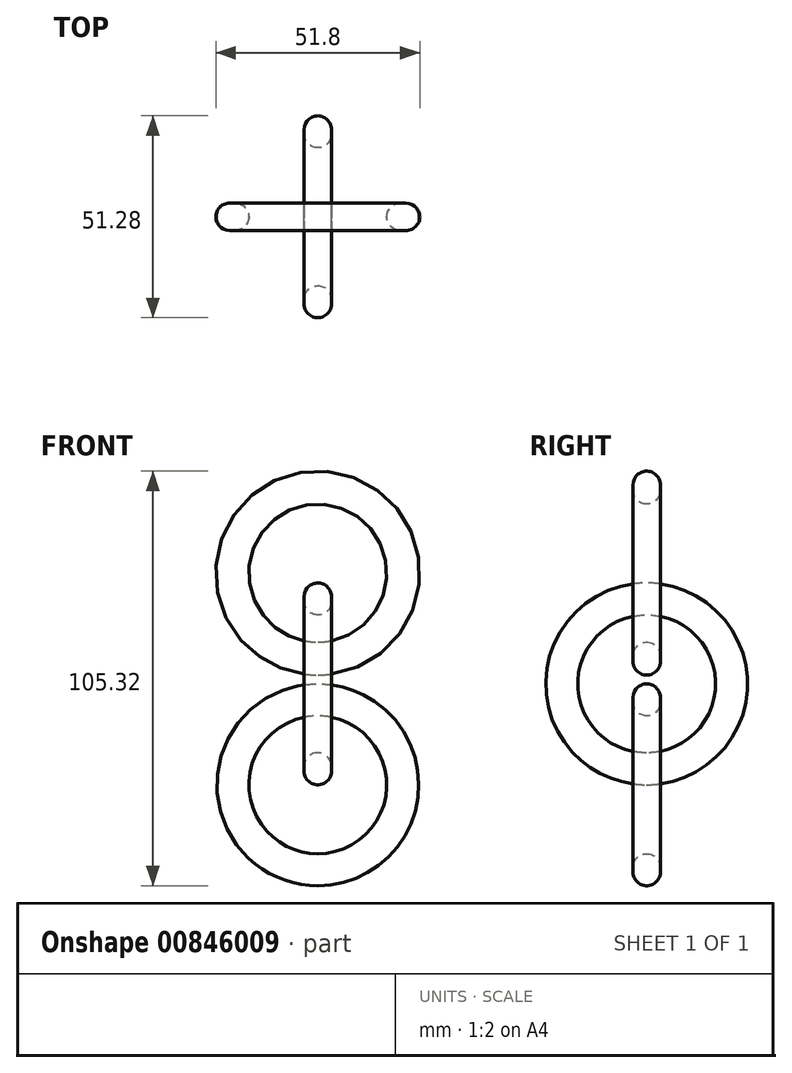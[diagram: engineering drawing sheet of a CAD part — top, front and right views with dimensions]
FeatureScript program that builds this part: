
annotation { "Feature Type Name" : "Feature", "Feature Type Description" : "" }
export const myFeature = defineFeature(function(context is Context, id is Id, definition is map)
    precondition{}
    {
        {
            var Q0;
            Q0=qCreatedBy(makeId("Right.planeOp"),FACE);
            var sketch = newSketch(context, id + "F0", { "sketchPlane" : qUnion([Q0])});
            skCircle(sketch, "E0", {"center": v(0, 0) * mm, "radius": 25.64 * mm});
            skCircle(sketch, "E1", {"center": v(0, 0) * mm, "radius": 17.51 * mm});
            skSolve(sketch);
        }
        {
            var Q0;
            Q0=makeQuery(id+"F0.imprint","IMPRINT",FACE,{"disambiguationData":[TD([[makeQuery(id+"F0.imprint","IMPRINT",EDGE,{"derivedFrom":sQuery(id+"F0.wireOp",EDGE,"E0")}),1.0]])]});
            extrude(context, id + "F1", {"entities" : qUnion([Q0]), "endBound" : BoundingType.SYMMETRIC, "depth" : 7 * mm, "offsetDistance" : 25 * mm});
        }
        {
            var Q0;
            Q0=qCreatedBy(makeId("Front.planeOp"),FACE);
            var sketch = newSketch(context, id + "F2", { "sketchPlane" : qUnion([Q0])});
            skCircle(sketch, "E2", {"center": v(0, -25.64) * mm, "radius": 25.64 * mm});
            skCircle(sketch, "E3", {"center": v(0, -25.64) * mm, "radius": 17.5 * mm});
            skSolve(sketch);
        }
        {
            var Q0;
            Q0=makeQuery(id+"F2.imprint","IMPRINT",FACE,{"disambiguationData":[TD([[makeQuery(id+"F2.imprint","IMPRINT",EDGE,{"derivedFrom":sQuery(id+"F2.wireOp",EDGE,"E2")}),1.0]])]});
            extrude(context, id + "F3", {"entities" : qUnion([Q0]), "endBound" : BoundingType.SYMMETRIC, "depth" : 7 * mm, "offsetDistance" : 25 * mm});
        }
        {
            var Q0;
            Q0=qCreatedBy(makeId("Front.planeOp"),FACE);
            var sketch = newSketch(context, id + "F4", { "sketchPlane" : qUnion([Q0])});
            skCircle(sketch, "E4", {"center": v(0, 28.15) * mm, "radius": 25.9 * mm});
            skCircle(sketch, "E5", {"center": v(0, 28.15) * mm, "radius": 17.54 * mm});
            skSolve(sketch);
        }
        {
            var Q0;
            Q0=makeQuery(id+"F4.imprint","IMPRINT",FACE,{"disambiguationData":[TD([[makeQuery(id+"F4.imprint","IMPRINT",EDGE,{"derivedFrom":sQuery(id+"F4.wireOp",EDGE,"E4")}),1.0]])]});
            extrude(context, id + "F5", {"entities" : qUnion([Q0]), "endBound" : BoundingType.SYMMETRIC, "depth" : 7 * mm, "offsetDistance" : 25 * mm});
        }
        {
            var Q0;
            Q0=makeQuery(id+"F5.opExtrude","CAP_EDGE",EDGE,{"disambiguationData":[OSD([sQuery(id+"F4.wireOp",EDGE,"E4")])],"isStart":false});
            var Q1;
            Q1=makeQuery(id+"F5.opExtrude","CAP_EDGE",EDGE,{"disambiguationData":[OSD([sQuery(id+"F4.wireOp",EDGE,"E4")])],"isStart":true});
            var Q2;
            Q2=makeQuery(id+"F5.opExtrude","SWEPT_FACE",FACE,{"disambiguationData":[OSD([sQuery(id+"F4.wireOp",EDGE,"E5")])]});
            var Q3;
            Q3=makeQuery(id+"F3.opExtrude","SWEPT_FACE",FACE,{"disambiguationData":[OSD([sQuery(id+"F2.wireOp",EDGE,"E3")])]});
            var Q4;
            Q4=makeQuery(id+"F3.opExtrude","SWEPT_FACE",FACE,{"disambiguationData":[OSD([sQuery(id+"F2.wireOp",EDGE,"E2")])]});
            var Q5;
            Q5=makeQuery(id+"F1.opExtrude","CAP_FACE",FACE,{"disambiguationData":[OSD([sQuery(id+"F0.wireOp",EDGE,"E0"),sQuery(id+"F0.wireOp",EDGE,"E1")])],"isStart":false});
            var Q6;
            Q6=makeQuery(id+"F1.opExtrude","CAP_FACE",FACE,{"disambiguationData":[OSD([sQuery(id+"F0.wireOp",EDGE,"E0"),sQuery(id+"F0.wireOp",EDGE,"E1")])],"isStart":true});
            fillet(context, id + "F6", {"entities" : qUnion([Q0, Q1, Q2, Q3, Q4, Q5, Q6]), "radius" : 3.5 * mm, "tangentPropagation" : true, "allowEdgeOverflow" : false});
        }
    });
